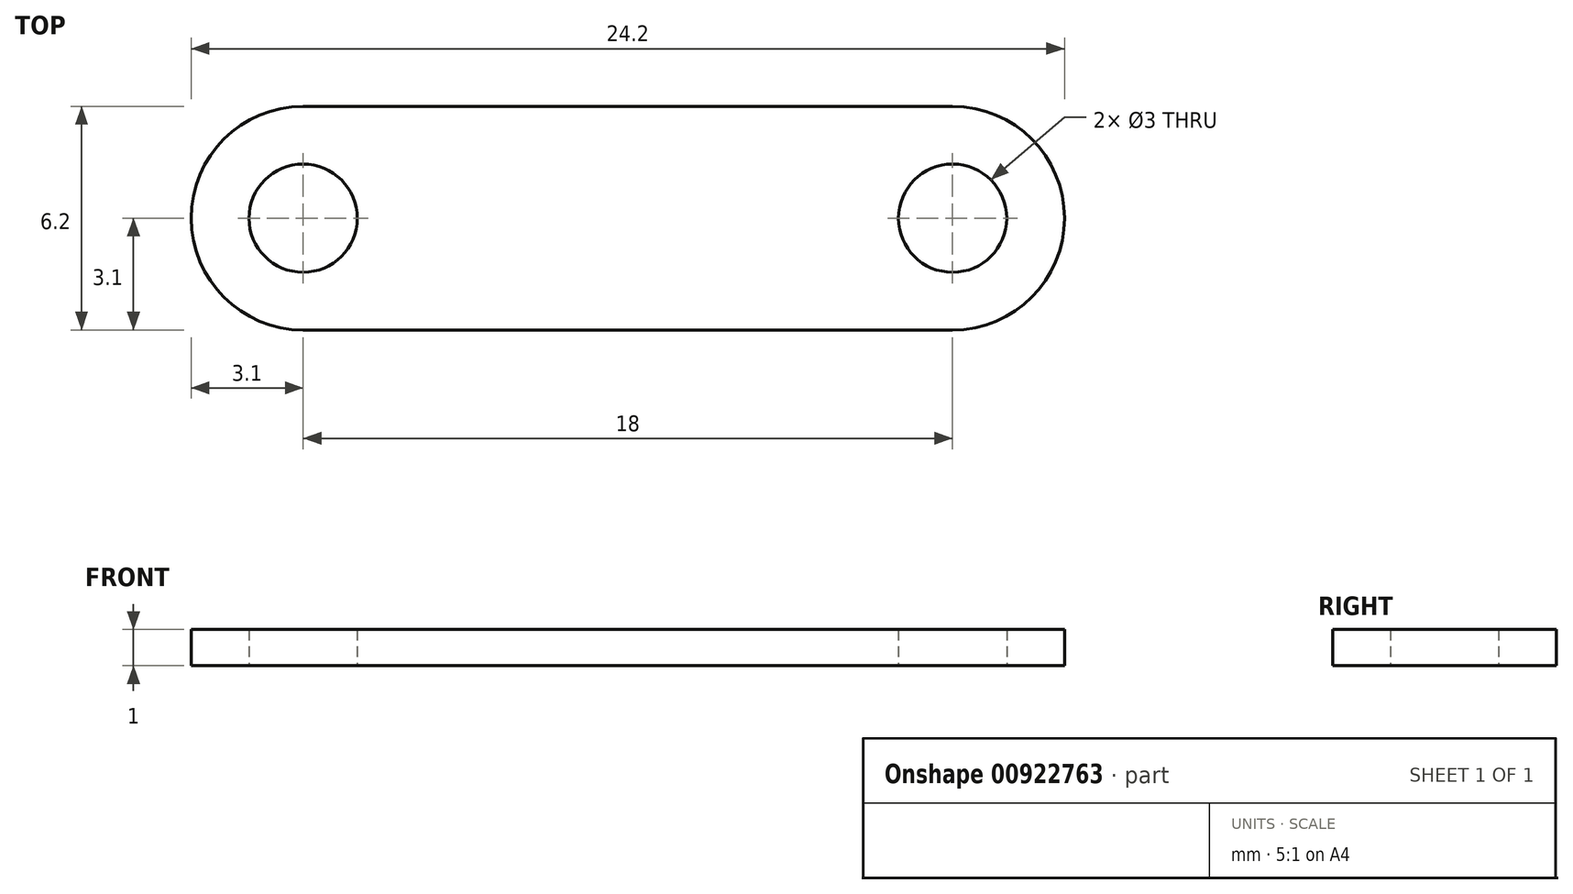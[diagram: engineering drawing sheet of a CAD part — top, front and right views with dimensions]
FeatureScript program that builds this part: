
annotation { "Feature Type Name" : "Feature", "Feature Type Description" : "" }
export const myFeature = defineFeature(function(context is Context, id is Id, definition is map)
    precondition{}
    {
        {
            var Q0;
            Q0=qCreatedBy(makeId("Top.planeOp"),FACE);
            var sketch = newSketch(context, id + "F0", { "sketchPlane" : qUnion([Q0])});
            skCircle(sketch, "E0", {"center": v(-9, 0) * mm, "radius": 1.5 * mm});
            skCircle(sketch, "E1.MirrorC", {"center": v(9, 0) * mm, "radius": 1.5 * mm});
            skLineSegment(sketch, "E2", {"start": v(-9, 0) * mm, "end": v(9, 0) * mm, "construction": true});
            skArc(sketch, "E3.0.startCap", {"start": v(-9, -3.1) * mm, "mid": v(-12.1, 0) * mm, "end": v(-9, 3.1) * mm});
            skArc(sketch, "E3.0.endCap", {"start": v(9, 3.1) * mm, "mid": v(12.1, 0) * mm, "end": v(9, -3.1) * mm});
            skLineSegment(sketch, "E3.0.left", {"start": v(-9, 3.1) * mm, "end": v(9, 3.1) * mm});
            skLineSegment(sketch, "E3.0.right", {"start": v(-9, -3.1) * mm, "end": v(9, -3.1) * mm});
            skSolve(sketch);
        }
        {
            var Q0;
            Q0 = qSketchRegion(id + "F0", true);
            extrude(context, id + "F1", {"entities" : qUnion([Q0]), "depth" : 1 * mm, "offsetDistance" : 25 * mm});
        }
    });
